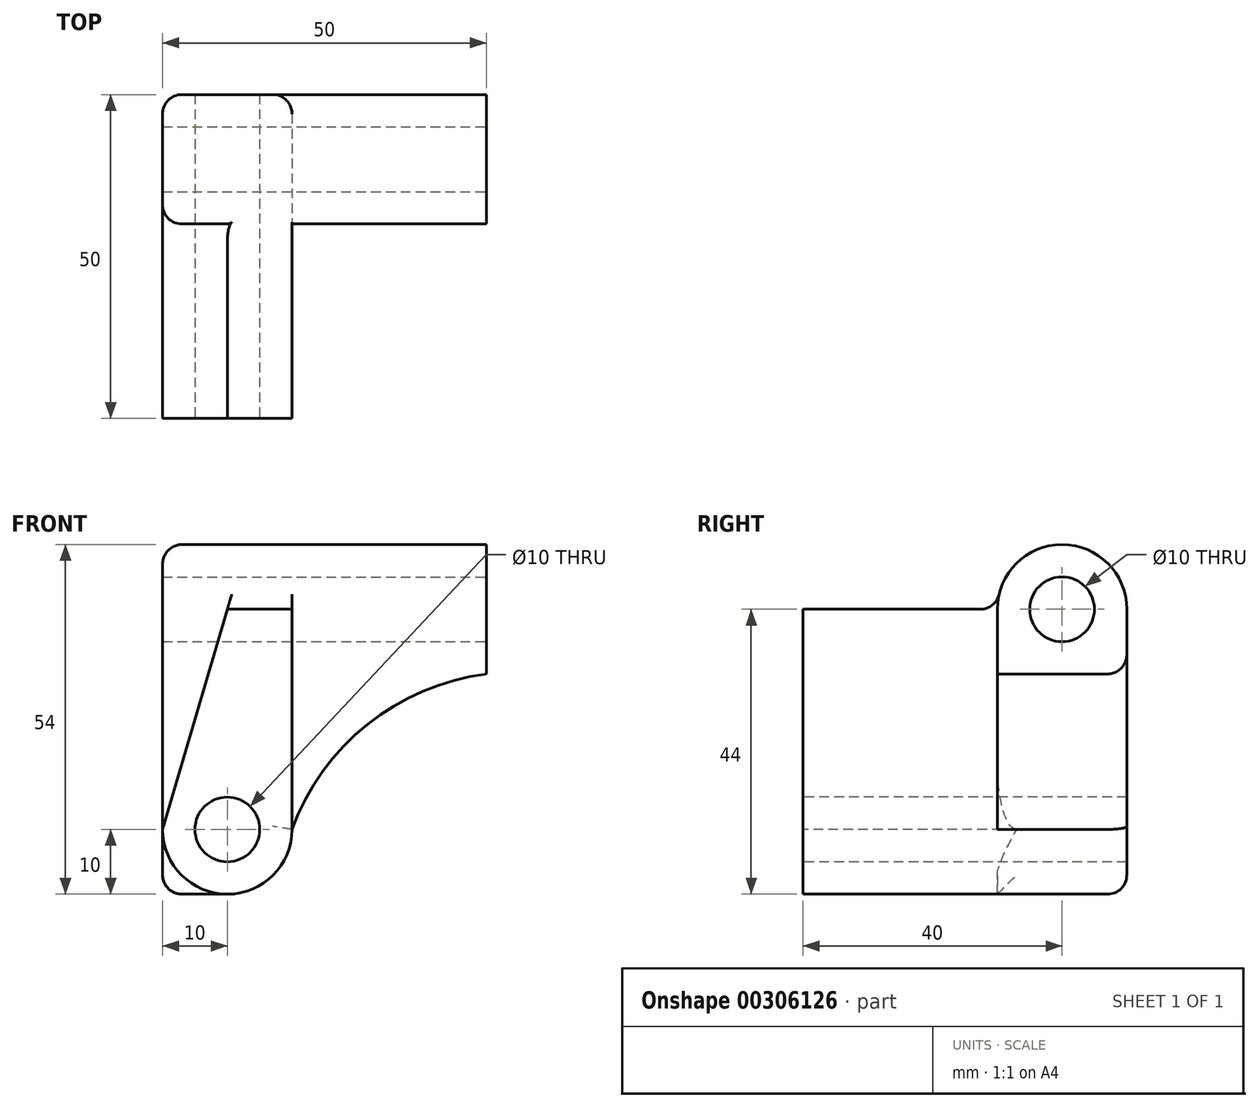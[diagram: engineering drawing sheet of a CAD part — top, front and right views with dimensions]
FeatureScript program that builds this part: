
annotation { "Feature Type Name" : "Feature", "Feature Type Description" : "" }
export const myFeature = defineFeature(function(context is Context, id is Id, definition is map)
    precondition{}
    {
        {
            var Q0;
            Q0=qCreatedBy(makeId("Front.planeOp"),FACE);
            var sketch = newSketch(context, id + "F0", { "sketchPlane" : qUnion([Q0])});
            skLineSegment(sketch, "E0.bottom", {"start": v(0, 0) * mm, "end": v(50, 0) * mm});
            skLineSegment(sketch, "E0.top", {"start": v(0, 54) * mm, "end": v(50, 54) * mm});
            skLineSegment(sketch, "E0.left", {"start": v(0, 0) * mm, "end": v(0, 54) * mm});
            skLineSegment(sketch, "E0.right", {"start": v(50, 0) * mm, "end": v(50, 54) * mm});
            skCircle(sketch, "E1", {"center": v(10, 10) * mm, "radius": 5 * mm});
            skSolve(sketch);
        }
        {
            var Q0;
            Q0=makeQuery(id+"F0.imprint","IMPRINT",FACE,{"disambiguationData":[TD([[makeQuery(id+"F0.imprint","IMPRINT",EDGE,{"derivedFrom":sQuery(id+"F0.wireOp",EDGE,"E0.bottom")}),1.0]])]});
            extrude(context, id + "F1", {"entities" : qUnion([Q0]), "oppositeDirection" : true, "depth" : 50 * mm});
        }
        {
            var Q0;
            Q0=makeQuery(id+"F1.opExtrude","SWEPT_FACE",FACE,{"disambiguationData":[OSD([sQuery(id+"F0.wireOp",EDGE,"E0.right")])]});
            var sketch = newSketch(context, id + "F2", { "sketchPlane" : qUnion([Q0])});
            skCircle(sketch, "E2", {"center": v(40, 44) * mm, "radius": 5 * mm});
            skSolve(sketch);
        }
        {
            var Q0;
            Q0=makeQuery(id+"F2.imprint","IMPRINT",FACE,{"disambiguationData":[TD([[makeQuery(id+"F2.imprint","IMPRINT",EDGE,{"derivedFrom":sQuery(id+"F2.wireOp",EDGE,"E2")}),1.0]])]});
            extrude(context, id + "F3", {"entities" : qUnion([Q0]), "operationType" : NewBodyOperationType.REMOVE, "endBound" : BoundingType.THROUGH_ALL, "oppositeDirection" : true, "depth" : 25 * mm});
        }
        {
            var Q0;
            Q0=makeQuery(id+"F1.opExtrude","CAP_FACE",FACE,{"disambiguationData":[OSD([sQuery(id+"F0.wireOp",EDGE,"E0.bottom"),sQuery(id+"F0.wireOp",EDGE,"E0.top"),sQuery(id+"F0.wireOp",EDGE,"E0.left"),sQuery(id+"F0.wireOp",EDGE,"E0.right"),sQuery(id+"F0.wireOp",EDGE,"E1")])],"isStart":true});
            var sketch = newSketch(context, id + "F4", { "sketchPlane" : qUnion([Q0])});
            skLineSegment(sketch, "E3", {"start": v(20, 20) * mm, "end": v(20, 10) * mm});
            skLineSegment(sketch, "E4", {"start": v(20, 0) * mm, "end": v(50, 0) * mm});
            skLineSegment(sketch, "E5", {"start": v(50, 0) * mm, "end": v(50, 54) * mm});
            skLineSegment(sketch, "E6", {"start": v(50, 54) * mm, "end": v(0, 54) * mm});
            skLineSegment(sketch, "E7", {"start": v(0, 54) * mm, "end": v(0, 44) * mm});
            skArc(sketch, "E8", {"start": v(0, 10) * mm, "mid": v(10, 0) * mm, "end": v(20, 10) * mm});
            skLineSegment(sketch, "E9", {"start": v(50, 0) * mm, "end": v(0, 0) * mm});
            skLineSegment(sketch, "E10", {"start": v(0, 0) * mm, "end": v(0, 10) * mm});
            skLineSegment(sketch, "E11", {"start": v(20, 20) * mm, "end": v(20, 44) * mm});
            skLineSegment(sketch, "E12", {"start": v(20, 44) * mm, "end": v(10, 44) * mm});
            skLineSegment(sketch, "E13", {"start": v(10, 44) * mm, "end": v(0, 44) * mm});
            skLineSegment(sketch, "E14", {"start": v(10, 44) * mm, "end": v(0, 10) * mm});
            skSolve(sketch);
        }
        {
            var Q0;
            {var subQ7=sQuery(id+"F4.wireOp",EDGE,"E3");Q0=makeQuery(id+"F4.imprint","IMPRINT",FACE,{"disambiguationData":[TD([[makeQuery(id+"F4.imprint","IMPRINT",EDGE,{"derivedFrom":subQ7}),1.0]])]});}
            var Q1;
            {var subQ0=sQuery(id+"F4.wireOp",EDGE,"E13");Q1=makeQuery(id+"F4.imprint","IMPRINT",FACE,{"disambiguationData":[TD([[makeQuery(id+"F4.imprint","IMPRINT",EDGE,{"derivedFrom":subQ0}),1.0]])]});}
            var Q2;
            {var subQ0=sQuery(id+"F4.wireOp",EDGE,"E10");Q2=makeQuery(id+"F4.imprint","IMPRINT",FACE,{"disambiguationData":[TD([[makeQuery(id+"F4.imprint","IMPRINT",EDGE,{"derivedFrom":subQ0}),-1.0]])]});}
            extrude(context, id + "F5", {"entities" : qUnion([Q0, Q1, Q2]), "operationType" : NewBodyOperationType.REMOVE, "oppositeDirection" : true, "depth" : 30 * mm});
        }
        {
            var Q0;
            Q0=makeQuery(id+"F1.opExtrude","SWEPT_FACE",FACE,{"disambiguationData":[OSD([sQuery(id+"F0.wireOp",EDGE,"E0.right")])]});
            var sketch = newSketch(context, id + "F6", { "sketchPlane" : qUnion([Q0])});
            skCircle(sketch, "E15", {"center": v(40, 44) * mm, "radius": 10 * mm});
            skLineSegment(sketch, "E16", {"start": v(30, 54) * mm, "end": v(50, 54) * mm});
            skLineSegment(sketch, "E17", {"start": v(50, 54) * mm, "end": v(50, 44) * mm});
            skLineSegment(sketch, "E18", {"start": v(30, 54) * mm, "end": v(30, 44) * mm});
            skSolve(sketch);
        }
        {
            var Q0;
            {var subQ0=sQuery(id+"F6.wireOp",EDGE,"E18");Q0=makeQuery(id+"F6.imprint","IMPRINT",FACE,{"disambiguationData":[TD([[makeQuery(id+"F6.imprint","IMPRINT",EDGE,{"derivedFrom":subQ0}),-1.0]])]});}
            var Q1;
            {var subQ0=sQuery(id+"F6.wireOp",EDGE,"E17");Q1=makeQuery(id+"F6.imprint","IMPRINT",FACE,{"disambiguationData":[TD([[makeQuery(id+"F6.imprint","IMPRINT",EDGE,{"derivedFrom":subQ0}),1.0]])]});}
            extrude(context, id + "F7", {"entities" : qUnion([Q0, Q1]), "operationType" : NewBodyOperationType.REMOVE, "endBound" : BoundingType.THROUGH_ALL, "oppositeDirection" : true, "depth" : 25 * mm});
        }
        {
            var Q0;
            {var subQ0=sQuery(id+"F4.wireOp",EDGE,"E8");var subQ1=sQuery(id+"F4.wireOp",EDGE,"E3");var subQ2=sQuery(id+"F4.wireOp",EDGE,"E9");var subQ3=sQuery(id+"F4.wireOp",EDGE,"E11");var subQ7=sQuery(id+"F4.wireOp",EDGE,"E12");var subQ8=sQuery(id+"F4.wireOp",EDGE,"E5");Q0=makeQuery(id+"F7.boolean.opBoolean","SPLIT",FACE,{"disambiguationData":[TD([makeQuery(id+"F1.opExtrude","SWEPT_FACE",FACE,{"disambiguationData":[OSD([sQuery(id+"F0.wireOp",EDGE,"E0.bottom")])]})])],"derivedFrom":makeQuery(id+"F5.boolean.opBoolean","COPY",FACE,{"derivedFrom":makeQuery(id+"F5.opExtrude","CAP_FACE",FACE,{"disambiguationData":[OSD([subQ1,subQ8,sQuery(id+"F4.wireOp",EDGE,"E6"),sQuery(id+"F4.wireOp",EDGE,"E7"),subQ0,subQ2,sQuery(id+"F4.wireOp",EDGE,"E10"),subQ3,subQ7,sQuery(id+"F4.wireOp",EDGE,"h9BfFep8-FqUX-o5Tz-v7IK-gZ4OWpj35Uev")])],"isStart":false})})});}
            var sketch = newSketch(context, id + "F8", { "sketchPlane" : qUnion([Q0])});
            skPoint(sketch, "E19", {"position": v(50, 34) * mm});
            skPoint(sketch, "E20", {"position": v(20, 10) * mm});
            skArc(sketch, "E21", {"start": v(50, 34) * mm, "mid": v(31.63, 26.21) * mm, "end": v(20, 10) * mm});
            skSolve(sketch);
        }
        {
            var Q0;
            {var subQ0=sQuery(id+"F8.wireOp",EDGE,"E21");Q0=makeQuery(id+"F8.imprint","IMPRINT",FACE,{"disambiguationData":[TD([[makeQuery(id+"F8.imprint","IMPRINT",EDGE,{"derivedFrom":subQ0}),1.0]])]});}
            extrude(context, id + "F9", {"entities" : qUnion([Q0]), "operationType" : NewBodyOperationType.REMOVE, "oppositeDirection" : true, "depth" : 25 * mm});
        }
        {
            var Q0;
            Q0=makeQuery(id+"F5.boolean.opBoolean","COPY",EDGE,{"derivedFrom":makeQuery(id+"F5.opExtrude","CAP_EDGE",EDGE,{"disambiguationData":[OSD([sQuery(id+"F4.wireOp",EDGE,"E12")])],"isStart":true})});
            var Q1;
            Q1=makeQuery(id+"F5.boolean.opBoolean","COPY",EDGE,{"derivedFrom":makeQuery(id+"F5.opExtrude","CAP_EDGE",EDGE,{"disambiguationData":[OSD([sQuery(id+"F4.wireOp",EDGE,"E14")])],"isStart":true})});
            var Q2;
            Q2=makeQuery(id+"F7.boolean.opBoolean","MERGE",EDGE,{"derivedFrom":[makeQuery(id+"F5.boolean.opBoolean","COPY",EDGE,{"derivedFrom":makeQuery(id+"F5.opExtrude","CAP_EDGE",EDGE,{"disambiguationData":[OSD([sQuery(id+"F4.wireOp",EDGE,"E12")])],"isStart":false})}),makeQuery(id+"F7.opExtrude","SWEPT_EDGE",EDGE,{"disambiguationData":[OSD([sQuery(id+"F4.wireOp",EDGE,"E5"),sQuery(id+"F6.wireOp",EDGE,"E15"),sQuery(id+"F6.wireOp",EDGE,"E18")])]})]});
            var Q3;
            Q3=makeQuery(id+"F9.boolean.opBoolean","COPY",EDGE,{"derivedFrom":makeQuery(id+"F9.opExtrude","CAP_EDGE",EDGE,{"disambiguationData":[OSD([sQuery(id+"F8.wireOp",EDGE,"E21")])],"isStart":true})});
            var Q4;
            Q4=makeQuery(id+"F9.boolean.opBoolean","INTERSECT",EDGE,{"derivedFrom":[makeQuery(id+"F1.opExtrude","CAP_FACE",FACE,{"disambiguationData":[OSD([sQuery(id+"F0.wireOp",EDGE,"E0.bottom"),sQuery(id+"F0.wireOp",EDGE,"E0.top"),sQuery(id+"F0.wireOp",EDGE,"E0.left"),sQuery(id+"F0.wireOp",EDGE,"E0.right"),sQuery(id+"F0.wireOp",EDGE,"E1")])],"isStart":false}),makeQuery(id+"F9.opExtrude","SWEPT_FACE",FACE,{"disambiguationData":[OSD([sQuery(id+"F8.wireOp",EDGE,"E21")])]})]});
            var Q5;
            Q5=makeQuery(id+"F9.boolean.opBoolean","INTERSECT",EDGE,{"derivedFrom":[makeQuery(id+"F1.opExtrude","CAP_FACE",FACE,{"disambiguationData":[OSD([sQuery(id+"F0.wireOp",EDGE,"E0.bottom"),sQuery(id+"F0.wireOp",EDGE,"E0.top"),sQuery(id+"F0.wireOp",EDGE,"E0.left"),sQuery(id+"F0.wireOp",EDGE,"E0.right"),sQuery(id+"F0.wireOp",EDGE,"E1")])],"isStart":false}),makeQuery(id+"F9.opExtrude","SWEPT_FACE",FACE,{"disambiguationData":[OSD([sQuery(id+"F4.wireOp",EDGE,"E8")])]})]});
            var Q6;
            {var subQ0=sQuery(id+"F6.wireOp",EDGE,"E15");var subQ1=makeQuery(id+"F6.imprint","INTERSECT",VERTEX,{"derivedFrom":[subQ0,sQuery(id+"F6.wireOp",EDGE,"E16")]});Q6=makeQuery(id+"F7.boolean.opBoolean","TWEAK_EDGE",EDGE,{"derivedFrom":[makeQuery(id+"F7.opExtrude","CAP_EDGE",EDGE,{"disambiguationData":[OSD([subQ0]),TDD([makeQuery(id+"F6.imprint","IMPRINT",EDGE,{"disambiguationData":[TD([[subQ1,1.0]])],"derivedFrom":subQ0})])],"isStart":true}),makeQuery(id+"F7.opExtrude","CAP_EDGE",EDGE,{"disambiguationData":[OSD([subQ0]),TDD([makeQuery(id+"F6.imprint","IMPRINT",EDGE,{"disambiguationData":[TD([[subQ1,-1.0]])],"derivedFrom":subQ0})])],"isStart":true})]});}
            var Q7;
            Q7=makeQuery(id+"F9.boolean.opBoolean","COPY",EDGE,{"derivedFrom":makeQuery(id+"F9.opExtrude","SWEPT_EDGE",EDGE,{"disambiguationData":[OSD([sQuery(id+"F4.wireOp",EDGE,"E5"),sQuery(id+"F8.wireOp",EDGE,"E21")])]})});
            var Q8;
            {var subQ0=sQuery(id+"F6.wireOp",EDGE,"E15");var subQ1=makeQuery(id+"F6.imprint","INTERSECT",VERTEX,{"derivedFrom":[subQ0,sQuery(id+"F6.wireOp",EDGE,"E16")]});Q8=makeQuery(id+"F7.boolean.opBoolean","INTERSECT",EDGE,{"derivedFrom":[makeQuery(id+"F1.opExtrude","SWEPT_FACE",FACE,{"disambiguationData":[OSD([sQuery(id+"F0.wireOp",EDGE,"E0.left")])]}),makeQuery(id+"F7.opExtrude","SWEPT_FACE",FACE,{"disambiguationData":[OSD([subQ0]),TDD([makeQuery(id+"F6.imprint","IMPRINT",EDGE,{"disambiguationData":[TD([[subQ1,1.0]])],"derivedFrom":subQ0})])]}),makeQuery(id+"F7.opExtrude","SWEPT_FACE",FACE,{"disambiguationData":[OSD([subQ0]),TDD([makeQuery(id+"F6.imprint","IMPRINT",EDGE,{"disambiguationData":[TD([[subQ1,-1.0]])],"derivedFrom":subQ0})])]})]});}
            var Q9;
            Q9=makeQuery(id+"F1.opExtrude","CAP_EDGE",EDGE,{"disambiguationData":[OSD([sQuery(id+"F0.wireOp",EDGE,"E0.left")])],"isStart":false});
            var Q10;
            Q10=makeQuery(id+"F5.boolean.opBoolean","COPY",EDGE,{"derivedFrom":makeQuery(id+"F5.opExtrude","CAP_EDGE",EDGE,{"disambiguationData":[OSD([sQuery(id+"F0.wireOp",EDGE,"E0.left"),sQuery(id+"F4.wireOp",EDGE,"E7")])],"isStart":false})});
            var Q11;
            Q11=makeQuery(id+"F1.opExtrude","SWEPT_EDGE",EDGE,{"disambiguationData":[OSD([sQuery(id+"F0.wireOp",EDGE,"E0.bottom"),sQuery(id+"F0.wireOp",EDGE,"E0.left")])]});
            var Q12;
            {var subQ0=sQuery(id+"F4.wireOp",EDGE,"E8");var subQ1=makeQuery(id+"F4.imprint","INTERSECT",VERTEX,{"derivedFrom":[subQ0,sQuery(id+"F4.wireOp",EDGE,"E9")]});Q12=makeQuery(id+"F5.boolean.opBoolean","TWEAK_EDGE",EDGE,{"derivedFrom":[makeQuery(id+"F5.opExtrude","CAP_EDGE",EDGE,{"disambiguationData":[OSD([subQ0]),TDD([makeQuery(id+"F4.imprint","IMPRINT",EDGE,{"disambiguationData":[TD([[subQ1,1.0]])],"derivedFrom":subQ0})])],"isStart":true}),makeQuery(id+"F5.opExtrude","CAP_EDGE",EDGE,{"disambiguationData":[OSD([subQ0]),TDD([makeQuery(id+"F4.imprint","IMPRINT",EDGE,{"disambiguationData":[TD([[makeQuery(id+"F4.imprint","INTERSECT",VERTEX,{"derivedFrom":[sQuery(id+"F4.wireOp",EDGE,"E3"),subQ0]}),1.0]])],"derivedFrom":subQ0})])],"isStart":true})]});}
            fillet(context, id + "F10", {"entities" : qUnion([Q0, Q1, Q2, Q3, Q4, Q5, Q6, Q7, Q8, Q9, Q10, Q11, Q12]), "radius" : 3 * mm, "tangentPropagation" : true, "allowEdgeOverflow" : false});
        }
    });
